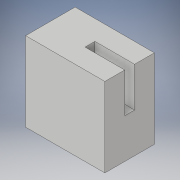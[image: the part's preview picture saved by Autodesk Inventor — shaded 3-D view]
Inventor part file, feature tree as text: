
AUTODESK INVENTOR PART (.ipt)
format: ipt  version: 2017 (Build 210142000, 142)  size: 112,128 bytes
history: native  units: in
note: dims shown in document units (in); Inventor stores cm internally (conversion verified against a paired STEP export)
features: extrude x2, sketch x2
ambient origin geometry x8: Origin, YZ Plane, XZ Plane, XY Plane, X Axis, Y Axis, Z Axis, Center Point
bodies: Solid1 (feature_tree)
feature tree (4):
  extrude  "Extrusion1"  Depth=0.25in
  extrude  "Extrusion2"  Depth=0.125in
  sketch  "Sketch1"  dims[d0=1.0in d1=0.25in]
  sketch  "Sketch2"  dims[d2=0.5in d3=0.125in d4=1.0in d5=0.25in d6=1.0in d7=0.0in d8=0.5in d9=0.5in d10=0.125in d11=0.0in]
